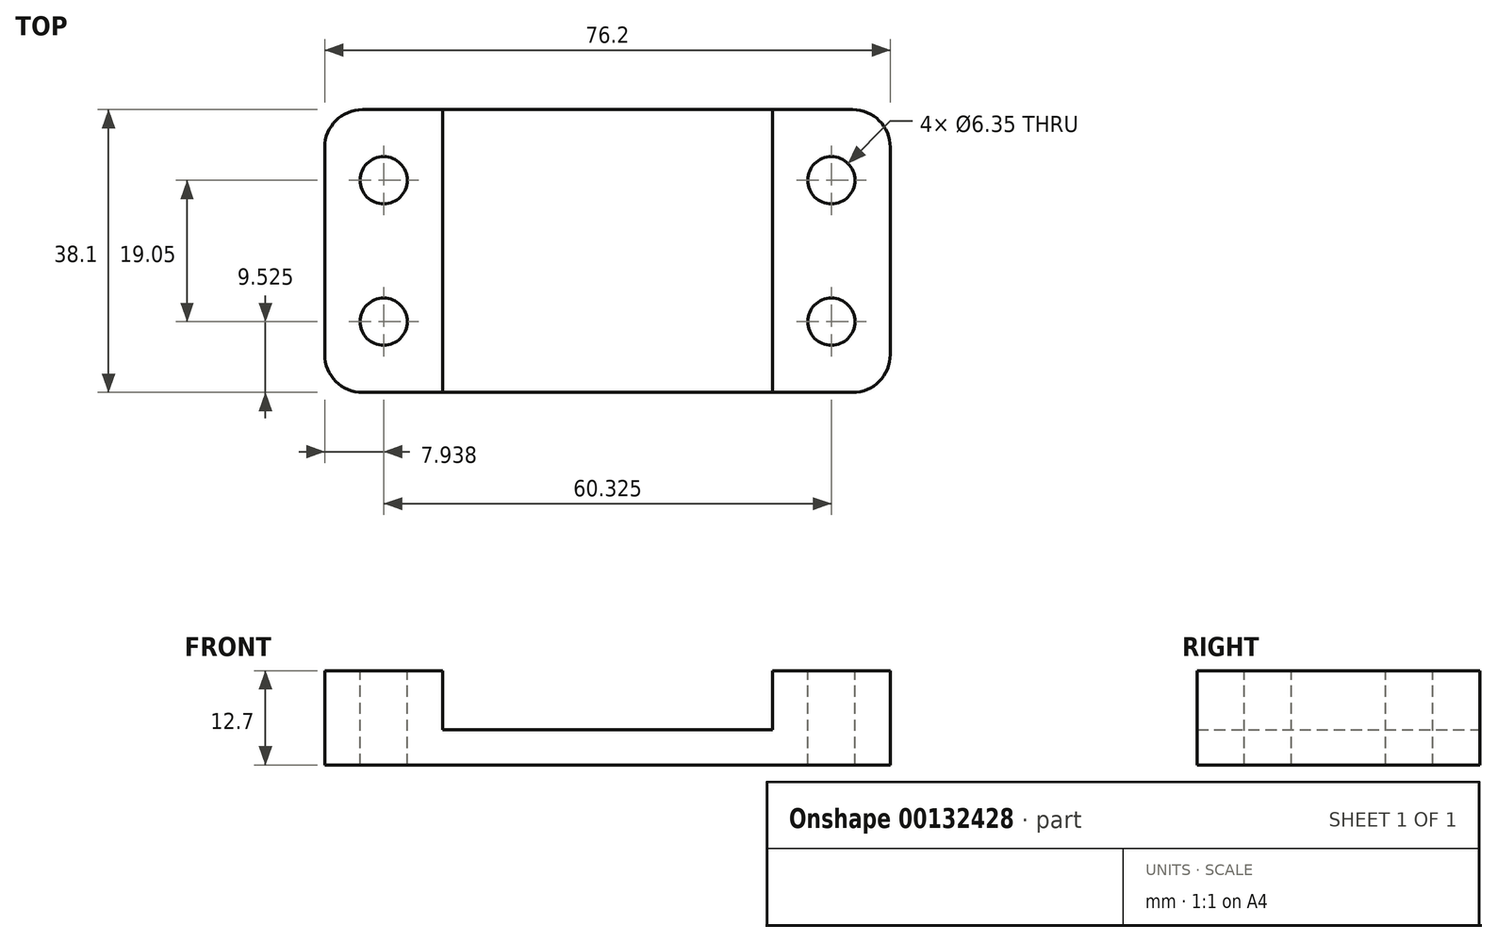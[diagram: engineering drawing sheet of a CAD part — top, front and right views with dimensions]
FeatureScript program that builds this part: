
annotation { "Feature Type Name" : "Feature", "Feature Type Description" : "" }
export const myFeature = defineFeature(function(context is Context, id is Id, definition is map)
    precondition{}
    {
        {
            var Q0;
            Q0=qCreatedBy(makeId("Front.planeOp"),FACE);
            var sketch = newSketch(context, id + "F0", { "sketchPlane" : qUnion([Q0])});
            skLineSegment(sketch, "E0.bottom", {"start": v(-22.23, 2.38) * mm, "end": v(22.23, 2.38) * mm});
            skLineSegment(sketch, "E0.top", {"start": v(-22.23, -2.38) * mm, "end": v(22.23, -2.38) * mm});
            skLineSegment(sketch, "E0.left", {"start": v(-22.23, 2.38) * mm, "end": v(-22.23, -2.38) * mm});
            skLineSegment(sketch, "E0.right", {"start": v(22.23, 2.38) * mm, "end": v(22.23, -2.38) * mm});
            skPoint(sketch, "E0.middle", {"position": v(0, 0) * mm});
            skLineSegment(sketch, "E1.bottom", {"start": v(-22.23, -2.38) * mm, "end": v(-38.1, -2.38) * mm});
            skLineSegment(sketch, "E1.top", {"start": v(-22.23, 10.32) * mm, "end": v(-38.1, 10.32) * mm});
            skLineSegment(sketch, "E1.left", {"start": v(-22.23, -2.38) * mm, "end": v(-22.23, 10.32) * mm});
            skLineSegment(sketch, "E1.right", {"start": v(-38.1, -2.38) * mm, "end": v(-38.1, 10.32) * mm});
            skLineSegment(sketch, "E2.bottom", {"start": v(22.23, -2.38) * mm, "end": v(38.1, -2.38) * mm});
            skLineSegment(sketch, "E2.top", {"start": v(22.22, 10.32) * mm, "end": v(38.1, 10.32) * mm});
            skLineSegment(sketch, "E2.left", {"start": v(22.23, -2.38) * mm, "end": v(22.23, 10.32) * mm});
            skLineSegment(sketch, "E2.right", {"start": v(38.1, -2.38) * mm, "end": v(38.1, 10.32) * mm});
            skSolve(sketch);
        }
        {
            var Q0;
            {var subQ3=sQuery(id+"F0.wireOp",EDGE,"E1.bottom");Q0=makeQuery(id+"F0.imprint","IMPRINT",FACE,{"disambiguationData":[TD([[makeQuery(id+"F0.imprint","IMPRINT",EDGE,{"derivedFrom":subQ3}),-1.0]])]});}
            var Q1;
            {var subQ0=sQuery(id+"F0.wireOp",EDGE,"E0.bottom");Q1=makeQuery(id+"F0.imprint","IMPRINT",FACE,{"disambiguationData":[TD([[makeQuery(id+"F0.imprint","IMPRINT",EDGE,{"derivedFrom":subQ0}),-1.0]])]});}
            var Q2;
            {var subQ3=sQuery(id+"F0.wireOp",EDGE,"E2.bottom");Q2=makeQuery(id+"F0.imprint","IMPRINT",FACE,{"disambiguationData":[TD([[makeQuery(id+"F0.imprint","IMPRINT",EDGE,{"derivedFrom":subQ3}),1.0]])]});}
            extrude(context, id + "F1", {"entities" : qUnion([Q0, Q1, Q2]), "depth" : 38.1 * mm});
        }
        {
            var Q0;
            Q0=makeQuery(id+"F1.opExtrude","SWEPT_FACE",FACE,{"disambiguationData":[OSD([sQuery(id+"F0.wireOp",EDGE,"E1.top")])]});
            var sketch = newSketch(context, id + "F2", { "sketchPlane" : qUnion([Q0])});
            skLineSegment(sketch, "E3", {"start": v(-30.16, 0) * mm, "end": v(-30.16, -9.53) * mm});
            skPoint(sketch, "E3.endSnap0", {"position": v(-30.16, -38.1) * mm});
            skLineSegment(sketch, "E4", {"start": v(-30.16, -9.53) * mm, "end": v(-30.16, -28.58) * mm});
            skLineSegment(sketch, "E5.0", {"start": v(22.23, -38.1) * mm, "end": v(22.23, 0) * mm});
            skLineSegment(sketch, "E6.0", {"start": v(38.1, -38.1) * mm, "end": v(38.1, 0) * mm});
            skLineSegment(sketch, "E7", {"start": v(22.23, 0) * mm, "end": v(38.1, 0) * mm});
            skLineSegment(sketch, "E8", {"start": v(30.16, 0) * mm, "end": v(30.16, -9.53) * mm});
            skLineSegment(sketch, "E9", {"start": v(30.16, -9.53) * mm, "end": v(30.16, -28.58) * mm});
            skSolve(sketch);
        }
        {
            var Q0;
            Q0=sQuery(id+"F2.wireOp",VERTEX,"E4.start");
            var Q1;
            Q1=sQuery(id+"F2.wireOp",VERTEX,"E4.end");
            var Q2;
            Q2=sQuery(id+"F2.wireOp",VERTEX,"E8.end");
            var Q3;
            Q3=sQuery(id+"F2.wireOp",VERTEX,"E9.end");
            var Q4;
            Q4=makeQuery(id+"F1.opExtrude","SWEPT_BODY",BODY,{"disambiguationData":[OSD([sQuery(id+"F0.wireOp",EDGE,"E0.bottom"),sQuery(id+"F0.wireOp",EDGE,"E0.top"),sQuery(id+"F0.wireOp",EDGE,"E1.bottom"),sQuery(id+"F0.wireOp",EDGE,"E1.top"),sQuery(id+"F0.wireOp",EDGE,"E1.left"),sQuery(id+"F0.wireOp",EDGE,"E1.right"),sQuery(id+"F0.wireOp",EDGE,"E2.bottom"),sQuery(id+"F0.wireOp",EDGE,"E2.top"),sQuery(id+"F0.wireOp",EDGE,"E2.left"),sQuery(id+"F0.wireOp",EDGE,"E2.right")])]});
            hole(context, id + "F3", {"style" : HoleStyle.SIMPLE, "endStyle" : HoleEndStyle.THROUGH, "holeDiameter" : 6.35 * mm, "locations" : qUnion([Q0, Q1, Q2, Q3]), "scope" : qUnion([Q4]), "isTappedThrough" : true});
        }
        {
            var Q0;
            Q0=makeQuery(id+"F1.opExtrude","CAP_EDGE",EDGE,{"disambiguationData":[OSD([sQuery(id+"F0.wireOp",EDGE,"E2.right")])],"isStart":true});
            var Q1;
            Q1=makeQuery(id+"F1.opExtrude","CAP_EDGE",EDGE,{"disambiguationData":[OSD([sQuery(id+"F0.wireOp",EDGE,"E2.right")])],"isStart":false});
            var Q2;
            Q2=makeQuery(id+"F1.opExtrude","CAP_EDGE",EDGE,{"disambiguationData":[OSD([sQuery(id+"F0.wireOp",EDGE,"E1.right")])],"isStart":true});
            var Q3;
            Q3=makeQuery(id+"F1.opExtrude","CAP_EDGE",EDGE,{"disambiguationData":[OSD([sQuery(id+"F0.wireOp",EDGE,"E1.right")])],"isStart":false});
            fillet(context, id + "F4", {"entities" : qUnion([Q0, Q1, Q2, Q3]), "radius" : 5.08 * mm, "tangentPropagation" : true, "allowEdgeOverflow" : false});
        }
    });
